# Revit family: QF_BPRO_RWR 3-A KS_573386
name_source: partatom
category: Sonderausstattung
revit_build: Autodesk Revit 2018 (Build: 20190510_1515(x64)
units: mm (PartAtom-declared; Revit-internal decimal feet)

## family parameters
Arbeitsebenenbasiert = Nein
Beim Laden mit Abzugskörper schneiden = Nein
Bemaßung runder Anschluss = Durchmesser verwenden
Gemeinsam genutzt = Nein
Immer vertikal = Ja
Raumberechnungspunkt = Ja
Teiletyp = Normal

## types (1)
- RWR 3-A KS
    Abstand Einlagen = 165 mm
    Anzahl Schienen = 3
    Artikel Nummer = 573386
    Beschreibung = Regalwagen aus rostfreiem Edelstahl
zum Einfahren in eine Kühlstation für die
Kaltportionierung am Speisenverteilband
Anzahl Auflagenpaare: 3 x 7 Paar (82 mm)
Gesamtkapazität: 27 GN 1/1- oder 54  GN 1/2
Tragfähigkeit: 80 kg
Stoßecken aus Kunststoff (Polyamid) an allen vier Ecken
    Beschreibung durch Hersteller analog Leistungsverzeichniskurztext = Abmessungen

Länge: 1.180 mm
Breite: 823 mm
Höhe: 1.200 mm
Abstand der Auflagenschienen: 82 mm

Ausführung

Der Regalwagen besteht aus CNS 18/10, Werkstoff-Nr. 1.4301.
Zwischen stabilem Vierkant-rohr mit 25 x 25 mm befinden sich
eingeschweißte U-Profil-Führungsschienen. Diese sind mit einer
Kippsicherung sowie einer Durchschubsicherung versehen.
Die jeweils 7 Auflagenpaare des dreiteiligen Wagens dienen
zum Einschieben von GN-Behältern, GN-Tabletts oder GN-Rosten.
Zusätzlich können 3 GN-Behälter der Größe GN 1/1 von oben
eingehängt werden. Der Wagen ist mit einem 10° schräg 
angebrachten Aufsatz versehen, welcher 3 GN-Behälter der 
Größe GN 1/1 (von oben eingehängt) aufnehmen kann.

Zur Vermeidung von Kälteverlusten ist der Regalwagen mit
einer durchgehenden Bodenplatte aus Edelstahl versehen. 

Der Regalwagen ist fahrbar mittels rostfreien Kunststoffrollen
gemäß DIN 18867, Teil 8
(4 Lenkrollen, davon 2 mit Feststeller, Rollendurchmesser 125 mm).
Wandabweiser aus Kunststoff (Polyamid) an allen vier Ecken schützen
vor Beschädigung.

Technische Daten

Werkstoff:		Chromnickelstahl 18/10,
		Polyamid (PA)
Gewicht:	38 kg
Tragfähigkeit je Wagen:	80 kg
Anzahl Auflagenpaare:	3 x 7 Stück
Kapazität:	27 x GN 1/1 oder
	54 x GN 1/2

Besonderheit

•	U-Profil-Führungsschienen mit Durchschubsicherung
•	3x GN-Behälter der Größe GN 1/1 können von oben 
eingehängt werden (optimal für die Portionierung am 
Speisenverteilband)
•	10° schräg angebrachter Aufsatz zur Aufnahme von 3 
GN-Behältern der Größe GN 1/1

Fabrikat

Hersteller:	B.PRO
Typ:                                       RWR 3-A KS
Best. Nr.:	573386
    Beschreibung durch Hersteller analog Leistungsverzeichnislangtext = Abmessungen

Länge: 1.180 mm
Breite: 823 mm
Höhe: 1.200 mm
Abstand der Auflagenschienen: 82 mm

Ausführung

Der Regalwagen besteht aus CNS 18/10, Werkstoff-Nr. 1.4301.
Zwischen stabilem Vierkant-rohr mit 25 x 25 mm befinden sich
eingeschweißte U-Profil-Führungsschienen. Diese sind mit einer
Kippsicherung sowie einer Durchschubsicherung versehen.
Die jeweils 7 Auflagenpaare des dreiteiligen Wagens dienen
zum Einschieben von GN-Behältern, GN-Tabletts oder GN-Rosten.
Zusätzlich können 3 GN-Behälter der Größe GN 1/1 von oben
eingehängt werden. Der Wagen ist mit einem 10° schräg 
angebrachten Aufsatz versehen, welcher 3 GN-Behälter der 
Größe GN 1/1 (von oben eingehängt) aufnehmen kann.

Zur Vermeidung von Kälteverlusten ist der Regalwagen mit
einer durchgehenden Bodenplatte aus Edelstahl versehen. 

Der Regalwagen ist fahrbar mittels rostfreien Kunststoffrollen
gemäß DIN 18867, Teil 8
(4 Lenkrollen, davon 2 mit Feststeller, Rollendurchmesser 125 mm).
Wandabweiser aus Kunststoff (Polyamid) an allen vier Ecken schützen
vor Beschädigung.

Technische Daten

Werkstoff:		Chromnickelstahl 18/10,
		Polyamid (PA)
Gewicht:	38 kg
Tragfähigkeit je Wagen:	80 kg
Anzahl Auflagenpaare:	3 x 7 Stück
Kapazität:	27 x GN 1/1 oder
	54 x GN 1/2

Besonderheit

•	U-Profil-Führungsschienen mit Durchschubsicherung
•	3x GN-Behälter der Größe GN 1/1 können von oben 
eingehängt werden (optimal für die Portionierung am 
Speisenverteilband)
•	10° schräg angebrachter Aufsatz zur Aufnahme von 3 
GN-Behältern der Größe GN 1/1

Fabrikat

Hersteller:	B.PRO
Typ:                                       RWR 3-A KS
Best. Nr.:	573386
    Gerätegewicht Netto = 38.00 kg
    Großküchengerätezuordnung = Ja
    Hersteller = B.PRO GmbH
    Höhe = 1200 mm
    Internetadresse Gerätehersteller = https://www.bpro-solutions.com
    Internetadresse für Ersatzteilliste = https://www.bpro-solutions.com
    Kosten = 0 $
    Länge Gerätebreite = 1180 mm  [stored 3.87139 ft]
    Material = QF_Metal-Stainless-Steel_general
    Material_Stoßschutz = QF_Rubber-Black-Matt
    Modell = RWR 3-A KS
    Sockelhöhe = 200 mm  [stored 0.656168 ft]
    Tiefe = 823 mm  [stored 2.70013 ft]
    Typenkommentare = Regalwagen RWR 3-A KS
    URL = https://www.bpro-solutions.com
    Versatz Einlage unten = 166 mm  [stored 0.544619 ft]

note: [stored X ft] marks values corroborated as IEEE doubles in the binary element streams (Revit-internal decimal feet)
